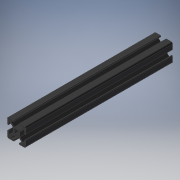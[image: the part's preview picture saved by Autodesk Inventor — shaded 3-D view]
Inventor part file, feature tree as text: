
AUTODESK INVENTOR PART (.ipt)
format: ipt  version: 2019 (Build 230136000, 136)  size: 238,592 bytes
history: native  units: mm
features: extrude x1, sketch x1
ambient origin geometry x8: Origin, YZ Plane, XZ Plane, XY Plane, X Axis, Y Axis, Z Axis, Center Point
bodies: Solid1 (feature_tree)
feature tree (2):
  extrude  "Extrusion1"  [1 undecoded]
  sketch  "Sketch_1"  dims[d0=160.0mm d1=0.0mm]
note: 1 required parameter value undecoded (feature->parameter linkage not recoverable at this tier; creation-order binding heuristic only, values carry confidence <= 0.55)
